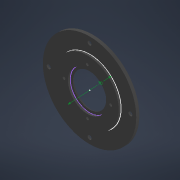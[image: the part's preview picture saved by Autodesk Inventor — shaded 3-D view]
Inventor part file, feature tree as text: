
AUTODESK INVENTOR PART (.ipt)
format: ipt  version: 2022 (Build 260153070, 153G)  size: 169,472 bytes
history: native  units: mm
features: sketch x5, hole x3, extrude x2, pattern_circular x2, other x1, chamfer x1
ambient origin geometry x8: Origin, YZ Plane, XZ Plane, XY Plane, X Axis, Y Axis, Z Axis, Center Point
bodies: Body1 (feature_tree)
feature tree (14):
  other  "Твердое тело1"
  extrude  "Выдавливание1"  Depth=104.0mm
  sketch  "Эскиз2"
  extrude  "Выдавливание2"  Depth=37.0mm
  chamfer  "Фаска1"  Distance=3.5mm
  hole  "Отверстие1"  [1 undecoded]
  hole  "Отверстие2"  [1 undecoded]
  pattern_circular  "Круговой массив1"  Angle=45.0deg  [1 undecoded]
  hole  "Отверстие3"  [1 undecoded]
  pattern_circular  "Круговой массив2"  Count=4 Angle=360.0deg
  sketch  "Эскиз1"
  sketch  "Эскиз3"
  sketch  "Эскиз4"
  sketch  "Эскиз5"
note: 4 required parameter values undecoded (feature->parameter linkage not recoverable at this tier; creation-order binding heuristic only, values carry confidence <= 0.55)
